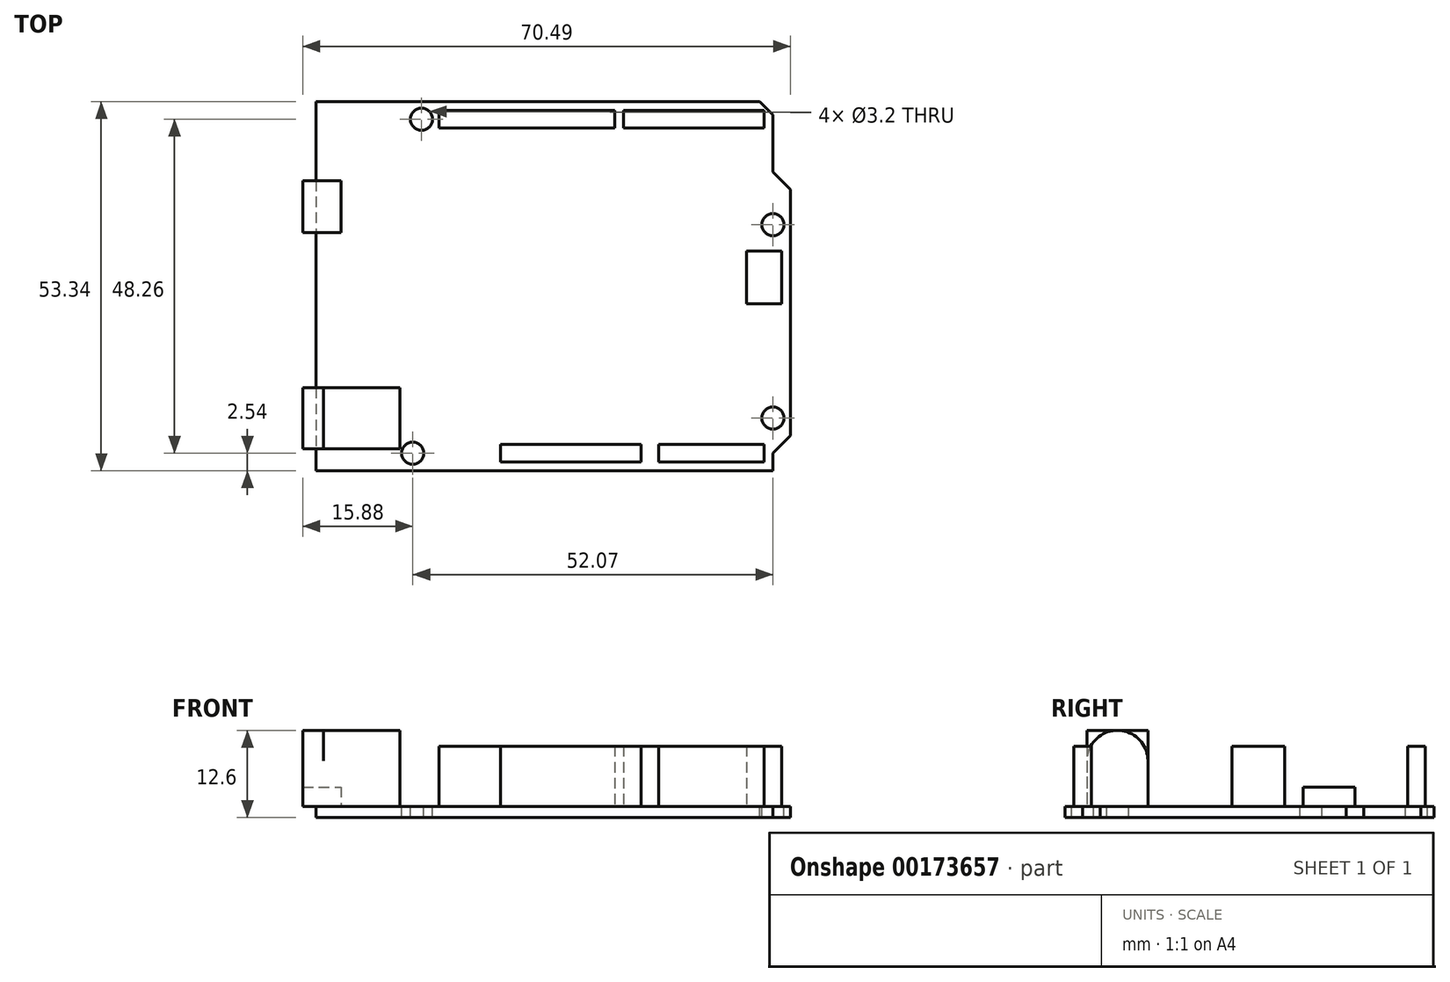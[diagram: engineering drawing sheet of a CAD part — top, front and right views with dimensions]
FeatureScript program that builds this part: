
annotation { "Feature Type Name" : "Feature", "Feature Type Description" : "" }
export const myFeature = defineFeature(function(context is Context, id is Id, definition is map)
    precondition{}
    {
        {
            var Q0;
            Q0=qCreatedBy(makeId("Top.planeOp"),FACE);
            var sketch = newSketch(context, id + "F0", { "sketchPlane" : qUnion([Q0])});
            skLineSegment(sketch, "E0", {"start": v(-13.97, 50.8) * mm, "end": v(-13.97, -2.54) * mm});
            skLineSegment(sketch, "E1", {"start": v(-13.97, -2.54) * mm, "end": v(52.07, -2.54) * mm});
            skLineSegment(sketch, "E2", {"start": v(52.07, -2.54) * mm, "end": v(52.07, 0) * mm});
            skLineSegment(sketch, "E3", {"start": v(52.07, 0) * mm, "end": v(54.61, 2.54) * mm});
            skLineSegment(sketch, "E4", {"start": v(54.61, 2.54) * mm, "end": v(54.61, 38.1) * mm});
            skLineSegment(sketch, "E5", {"start": v(52.07, 40.64) * mm, "end": v(54.61, 38.1) * mm});
            skLineSegment(sketch, "E6", {"start": v(52.07, 40.64) * mm, "end": v(52.07, 48.9) * mm});
            skLineSegment(sketch, "E7", {"start": v(52.07, 48.9) * mm, "end": v(50.16, 50.8) * mm});
            skLineSegment(sketch, "E8", {"start": v(50.16, 50.8) * mm, "end": v(-13.97, 50.8) * mm});
            skCircle(sketch, "E9", {"center": v(1.27, 48.26) * mm, "radius": 1.6 * mm});
            skCircle(sketch, "E10", {"center": v(0, 0) * mm, "radius": 1.6 * mm});
            skCircle(sketch, "E11", {"center": v(52.07, 5.08) * mm, "radius": 1.6 * mm});
            skCircle(sketch, "E12", {"center": v(52.07, 33.02) * mm, "radius": 1.6 * mm});
            skSolve(sketch);
        }
        {
            var Q0;
            Q0=makeQuery(id+"F0.imprint","IMPRINT",FACE,{"disambiguationData":[TD([[makeQuery(id+"F0.imprint","IMPRINT",EDGE,{"derivedFrom":sQuery(id+"F0.wireOp",EDGE,"E0")}),1.0]])]});
            extrude(context, id + "F1", {"entities" : qUnion([Q0]), "oppositeDirection" : true, "depth" : 1.6 * mm});
        }
        {
            var Q0;
            Q0=makeQuery(id+"F1.opExtrude","CAP_FACE",FACE,{"disambiguationData":[OSD([sQuery(id+"F0.wireOp",EDGE,"E0"),sQuery(id+"F0.wireOp",EDGE,"E1"),sQuery(id+"F0.wireOp",EDGE,"E2"),sQuery(id+"F0.wireOp",EDGE,"E3"),sQuery(id+"F0.wireOp",EDGE,"E4"),sQuery(id+"F0.wireOp",EDGE,"E5"),sQuery(id+"F0.wireOp",EDGE,"E6"),sQuery(id+"F0.wireOp",EDGE,"E7"),sQuery(id+"F0.wireOp",EDGE,"E8"),sQuery(id+"F0.wireOp",EDGE,"E9"),sQuery(id+"F0.wireOp",EDGE,"E10"),sQuery(id+"F0.wireOp",EDGE,"E11"),sQuery(id+"F0.wireOp",EDGE,"E12")])],"isStart":true});
            var sketch = newSketch(context, id + "F2", { "sketchPlane" : qUnion([Q0])});
            skLineSegment(sketch, "E13.bottom", {"start": v(3.8, 49.53) * mm, "end": v(29.2, 49.53) * mm});
            skLineSegment(sketch, "E13.top", {"start": v(3.8, 47) * mm, "end": v(29.2, 47) * mm});
            skLineSegment(sketch, "E13.left", {"start": v(3.8, 49.53) * mm, "end": v(3.8, 46.99) * mm});
            skLineSegment(sketch, "E13.right", {"start": v(29.2, 49.53) * mm, "end": v(29.2, 47) * mm});
            skLineSegment(sketch, "E14.bottom", {"start": v(30.48, 49.53) * mm, "end": v(50.8, 49.53) * mm});
            skLineSegment(sketch, "E14.top", {"start": v(30.48, 47) * mm, "end": v(50.8, 47) * mm});
            skLineSegment(sketch, "E14.left", {"start": v(30.48, 49.53) * mm, "end": v(30.48, 47) * mm});
            skLineSegment(sketch, "E14.right", {"start": v(50.8, 49.53) * mm, "end": v(50.8, 47) * mm});
            skLineSegment(sketch, "E15.bottom", {"start": v(35.56, 1.27) * mm, "end": v(50.8, 1.27) * mm});
            skLineSegment(sketch, "E15.top", {"start": v(35.56, -1.27) * mm, "end": v(50.8, -1.27) * mm});
            skLineSegment(sketch, "E15.left", {"start": v(35.56, 1.27) * mm, "end": v(35.56, -1.27) * mm});
            skLineSegment(sketch, "E15.right", {"start": v(50.8, 1.27) * mm, "end": v(50.8, -1.27) * mm});
            skLineSegment(sketch, "E16.bottom", {"start": v(12.7, 1.27) * mm, "end": v(33.02, 1.27) * mm});
            skLineSegment(sketch, "E16.top", {"start": v(12.7, -1.27) * mm, "end": v(33.02, -1.27) * mm});
            skLineSegment(sketch, "E16.left", {"start": v(12.7, 1.27) * mm, "end": v(12.7, -1.27) * mm});
            skLineSegment(sketch, "E16.right", {"start": v(33.02, 1.27) * mm, "end": v(33.02, -1.27) * mm});
            skLineSegment(sketch, "E17.bottom", {"start": v(-15.88, 39.37) * mm, "end": v(-10.38, 39.37) * mm});
            skLineSegment(sketch, "E17.top", {"start": v(-15.88, 31.87) * mm, "end": v(-10.38, 31.87) * mm});
            skLineSegment(sketch, "E17.left", {"start": v(-15.88, 39.37) * mm, "end": v(-15.88, 31.87) * mm});
            skLineSegment(sketch, "E17.right", {"start": v(-10.38, 39.37) * mm, "end": v(-10.38, 31.87) * mm});
            skLineSegment(sketch, "E18.bottom", {"start": v(-15.88, 9.43) * mm, "end": v(-1.88, 9.43) * mm});
            skLineSegment(sketch, "E18.top", {"start": v(-15.88, 0.63) * mm, "end": v(-1.88, 0.63) * mm});
            skLineSegment(sketch, "E18.left", {"start": v(-15.88, 9.43) * mm, "end": v(-15.88, 0.64) * mm});
            skLineSegment(sketch, "E18.right", {"start": v(-1.88, 9.43) * mm, "end": v(-1.88, 0.64) * mm});
            skLineSegment(sketch, "E19.bottom", {"start": v(48.26, 29.21) * mm, "end": v(53.34, 29.21) * mm});
            skLineSegment(sketch, "E19.top", {"start": v(48.26, 21.59) * mm, "end": v(53.34, 21.59) * mm});
            skLineSegment(sketch, "E19.left", {"start": v(48.26, 29.21) * mm, "end": v(48.26, 21.59) * mm});
            skLineSegment(sketch, "E19.right", {"start": v(53.34, 29.21) * mm, "end": v(53.34, 21.59) * mm});
            skSolve(sketch);
        }
        {
            var Q0;
            Q0=makeQuery(id+"F2.imprint","IMPRINT",FACE,{"disambiguationData":[TD([[makeQuery(id+"F2.imprint","IMPRINT",EDGE,{"derivedFrom":sQuery(id+"F2.wireOp",EDGE,"E13.bottom")}),-1.0]])]});
            var Q1;
            Q1=makeQuery(id+"F2.imprint","IMPRINT",FACE,{"disambiguationData":[TD([[makeQuery(id+"F2.imprint","IMPRINT",EDGE,{"derivedFrom":sQuery(id+"F2.wireOp",EDGE,"E14.bottom")}),-1.0]])]});
            var Q2;
            Q2=makeQuery(id+"F2.imprint","IMPRINT",FACE,{"disambiguationData":[TD([[makeQuery(id+"F2.imprint","IMPRINT",EDGE,{"derivedFrom":sQuery(id+"F2.wireOp",EDGE,"E15.bottom")}),-1.0]])]});
            var Q3;
            Q3=makeQuery(id+"F2.imprint","IMPRINT",FACE,{"disambiguationData":[TD([[makeQuery(id+"F2.imprint","IMPRINT",EDGE,{"derivedFrom":sQuery(id+"F2.wireOp",EDGE,"E16.bottom")}),-1.0]])]});
            var Q4;
            Q4=makeQuery(id+"F2.imprint","IMPRINT",FACE,{"disambiguationData":[TD([[makeQuery(id+"F2.imprint","IMPRINT",EDGE,{"derivedFrom":sQuery(id+"F2.wireOp",EDGE,"E19.bottom")}),-1.0]])]});
            extrude(context, id + "F3", {"entities" : qUnion([Q0, Q1, Q2, Q3, Q4]), "depth" : 8.7 * mm});
        }
        {
            var Q0;
            {var subQ0=sQuery(id+"F2.wireOp",EDGE,"E17.left");Q0=makeQuery(id+"F2.imprint","IMPRINT",FACE,{"disambiguationData":[TD([[makeQuery(id+"F2.imprint","IMPRINT",EDGE,{"derivedFrom":subQ0}),1.0]])]});}
            var Q1;
            {var subQ0=sQuery(id+"F2.wireOp",EDGE,"E17.right");Q1=makeQuery(id+"F2.imprint","IMPRINT",FACE,{"disambiguationData":[TD([[makeQuery(id+"F2.imprint","IMPRINT",EDGE,{"derivedFrom":subQ0}),-1.0]])]});}
            extrude(context, id + "F4", {"entities" : qUnion([Q0, Q1]), "depth" : 2.8 * mm});
        }
        {
            var Q0;
            {var subQ0=sQuery(id+"F2.wireOp",EDGE,"E18.right");Q0=makeQuery(id+"F2.imprint","IMPRINT",FACE,{"disambiguationData":[TD([[makeQuery(id+"F2.imprint","IMPRINT",EDGE,{"derivedFrom":subQ0}),-1.0]])]});}
            var Q1;
            {var subQ0=sQuery(id+"F2.wireOp",EDGE,"E18.left");Q1=makeQuery(id+"F2.imprint","IMPRINT",FACE,{"disambiguationData":[TD([[makeQuery(id+"F2.imprint","IMPRINT",EDGE,{"derivedFrom":subQ0}),1.0]])]});}
            extrude(context, id + "F5", {"entities" : qUnion([Q0, Q1]), "depth" : 11 * mm});
        }
        {
            var Q0;
            Q0=makeQuery(id+"F5.opExtrude","SWEPT_FACE",FACE,{"disambiguationData":[OSD([sQuery(id+"F2.wireOp",EDGE,"E18.right")])]});
            var sketch = newSketch(context, id + "F6", { "sketchPlane" : qUnion([Q0])});
            skArc(sketch, "E20", {"start": v(9.43, 6.6) * mm, "mid": v(5.03, 11) * mm, "end": v(0.64, 6.6) * mm});
            skSolve(sketch);
        }
        {
            var Q0;
            {var subQ0=sQuery(id+"F6.wireOp",EDGE,"E20");var subQ1=sQuery(id+"F2.wireOp",EDGE,"E18.right");var subQ4=makeQuery(id+"F5.opExtrude","CAP_EDGE",EDGE,{"disambiguationData":[OSD([subQ1])],"isStart":false});var subQ5=makeQuery(id+"F6.imprint","INTERSECT",VERTEX,{"derivedFrom":[subQ4,subQ0]});Q0=makeQuery(id+"F6.imprint","IMPRINT",FACE,{"disambiguationData":[TD([[makeQuery(id+"F6.imprint","IMPRINT",EDGE,{"disambiguationData":[TD([[subQ5,-1.0]])],"derivedFrom":subQ0}),-1.0]])]});}
            var Q1;
            {var subQ0=sQuery(id+"F6.wireOp",EDGE,"E20");var subQ1=sQuery(id+"F2.wireOp",EDGE,"E18.right");var subQ4=makeQuery(id+"F5.opExtrude","CAP_EDGE",EDGE,{"disambiguationData":[OSD([subQ1])],"isStart":false});var subQ5=makeQuery(id+"F6.imprint","INTERSECT",VERTEX,{"derivedFrom":[subQ4,subQ0]});Q1=makeQuery(id+"F6.imprint","IMPRINT",FACE,{"disambiguationData":[TD([[makeQuery(id+"F6.imprint","IMPRINT",EDGE,{"disambiguationData":[TD([[subQ5,1.0]])],"derivedFrom":subQ0}),-1.0]])]});}
            extrude(context, id + "F7", {"entities" : qUnion([Q0, Q1]), "operationType" : NewBodyOperationType.REMOVE, "oppositeDirection" : true, "depth" : 11 * mm});
        }
    });
